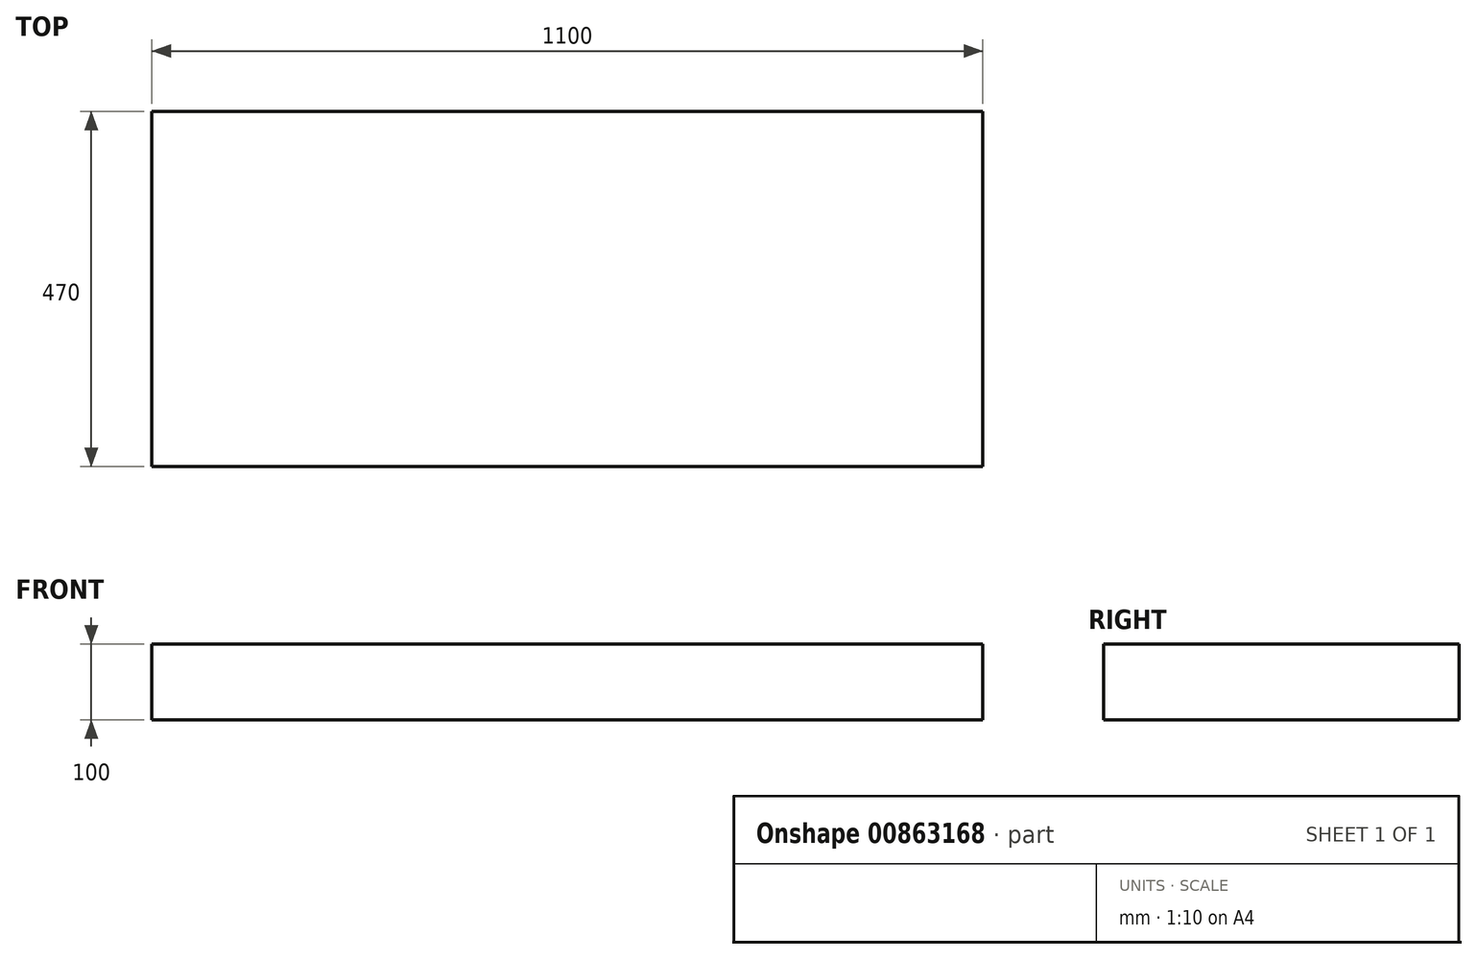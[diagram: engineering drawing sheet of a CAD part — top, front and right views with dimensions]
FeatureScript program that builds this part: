
annotation { "Feature Type Name" : "Feature", "Feature Type Description" : "" }
export const myFeature = defineFeature(function(context is Context, id is Id, definition is map)
    precondition{}
    {
        {
            var Q0;
            Q0=qCreatedBy(makeId("Top.planeOp"),FACE);
            var sketch = newSketch(context, id + "F0", { "sketchPlane" : qUnion([Q0])});
            skLineSegment(sketch, "E0", {"start": v(0, 0) * mm, "end": v(0, 470) * mm});
            skLineSegment(sketch, "E1", {"start": v(0, 470) * mm, "end": v(1100, 470) * mm});
            skLineSegment(sketch, "E2", {"start": v(1100, 470) * mm, "end": v(1100, 0) * mm});
            skLineSegment(sketch, "E3", {"start": v(1100, 0) * mm, "end": v(0, 0) * mm});
            skSolve(sketch);
        }
        {
            var Q0;
            Q0=makeQuery(id+"F0.imprint","IMPRINT",FACE,{"disambiguationData":[TD([[makeQuery(id+"F0.imprint","IMPRINT",EDGE,{"derivedFrom":sQuery(id+"F0.wireOp",EDGE,"E0")}),-1.0]])]});
            extrude(context, id + "F1", {"entities" : qUnion([Q0]), "depth" : 100 * mm, "offsetDistance" : 25 * mm});
        }
    });
